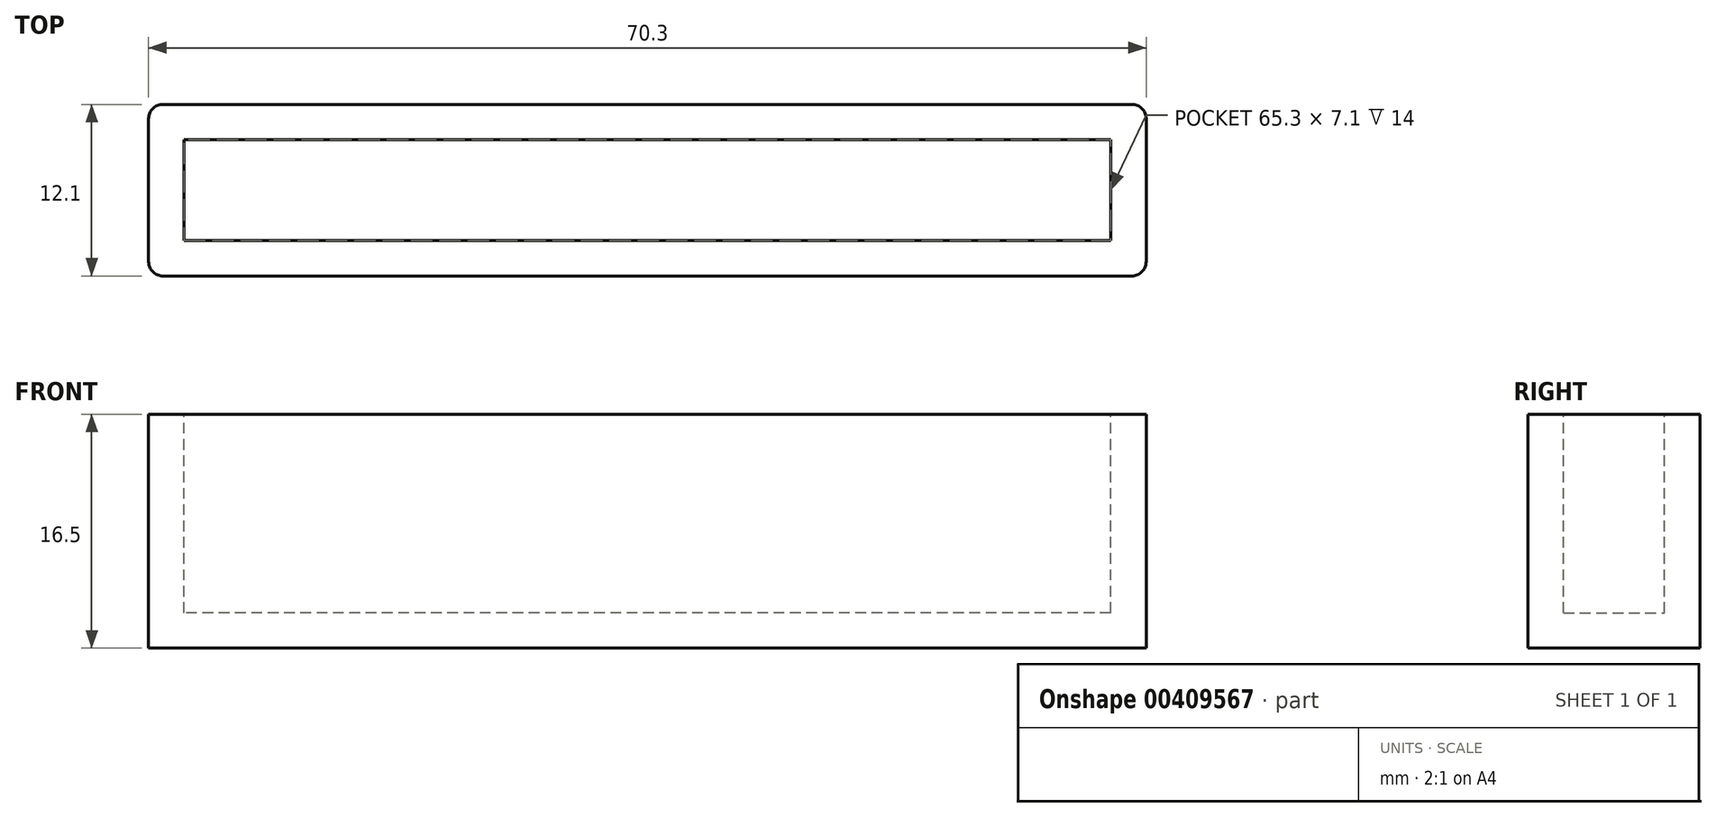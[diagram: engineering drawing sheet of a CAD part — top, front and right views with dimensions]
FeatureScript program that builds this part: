
annotation { "Feature Type Name" : "Feature", "Feature Type Description" : "" }
export const myFeature = defineFeature(function(context is Context, id is Id, definition is map)
    precondition{}
    {
        {
            var Q0;
            Q0=qCreatedBy(makeId("Front.planeOp"),FACE);
            var sketch = newSketch(context, id + "F0", { "sketchPlane" : qUnion([Q0])});
            skLineSegment(sketch, "E0.bottom", {"start": v(35.15, -8.25) * mm, "end": v(-35.15, -8.25) * mm});
            skLineSegment(sketch, "E0.top", {"start": v(35.15, 8.25) * mm, "end": v(-35.15, 8.25) * mm});
            skLineSegment(sketch, "E0.left", {"start": v(35.15, -8.25) * mm, "end": v(35.15, 8.25) * mm});
            skLineSegment(sketch, "E0.right", {"start": v(-35.15, -8.25) * mm, "end": v(-35.15, 8.25) * mm});
            skPoint(sketch, "E0.middle", {"position": v(0, 0) * mm});
            skSolve(sketch);
        }
        {
            var Q0;
            Q0 = qSketchRegion(id + "F0", true);
            extrude(context, id + "F1", {"entities" : qUnion([Q0]), "depth" : 12.1 * mm});
        }
        {
            var Q0;
            Q0=makeQuery(id+"F1.opExtrude","SWEPT_FACE",FACE,{"disambiguationData":[OSD([sQuery(id+"F0.wireOp",EDGE,"E0.top")])]});
            shell(context, id + "F2", {"entities" : qUnion([Q0]), "thickness" : 2.5 * mm});
        }
        {
            var Q0;
            Q0=makeQuery(id+"F1.opExtrude","CAP_EDGE",EDGE,{"disambiguationData":[OSD([sQuery(id+"F0.wireOp",EDGE,"E0.right")])],"isStart":false});
            var Q1;
            Q1=makeQuery(id+"F1.opExtrude","CAP_EDGE",EDGE,{"disambiguationData":[OSD([sQuery(id+"F0.wireOp",EDGE,"E0.left")])],"isStart":false});
            var Q2;
            Q2=makeQuery(id+"F1.opExtrude","CAP_EDGE",EDGE,{"disambiguationData":[OSD([sQuery(id+"F0.wireOp",EDGE,"E0.left")])],"isStart":true});
            var Q3;
            Q3=makeQuery(id+"F1.opExtrude","CAP_EDGE",EDGE,{"disambiguationData":[OSD([sQuery(id+"F0.wireOp",EDGE,"E0.right")])],"isStart":true});
            fillet(context, id + "F3", {"entities" : qUnion([Q0, Q1, Q2, Q3]), "radius" : 1 * mm, "tangentPropagation" : true, "allowEdgeOverflow" : false});
        }
    });
